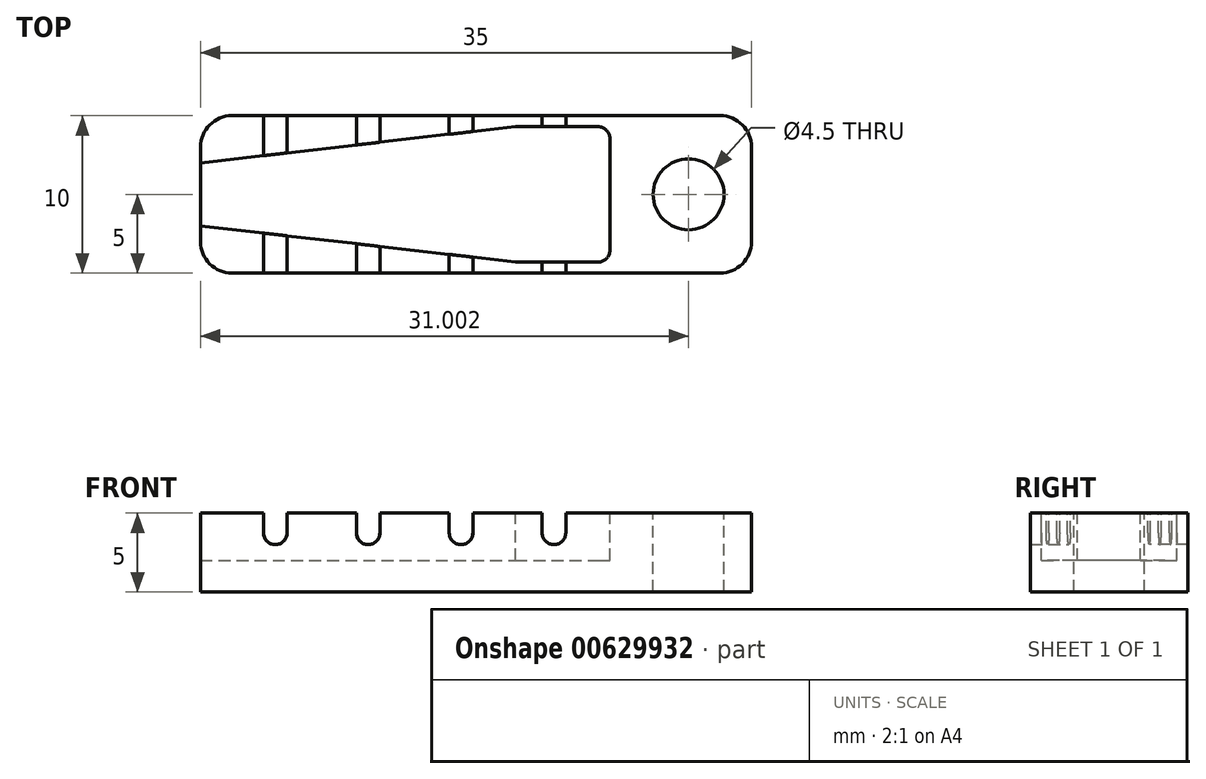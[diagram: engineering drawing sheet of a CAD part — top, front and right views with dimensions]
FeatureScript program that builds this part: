
annotation { "Feature Type Name" : "Feature", "Feature Type Description" : "" }
export const myFeature = defineFeature(function(context is Context, id is Id, definition is map)
    precondition{}
    {
        {
            var Q0;
            Q0=qCreatedBy(makeId("Top.planeOp"),FACE);
            var sketch = newSketch(context, id + "F0", { "sketchPlane" : qUnion([Q0])});
            skLineSegment(sketch, "E0.bottom", {"start": v(-22.89, 5) * mm, "end": v(12.11, 5) * mm});
            skLineSegment(sketch, "E0.top", {"start": v(-22.89, -5) * mm, "end": v(12.11, -5) * mm});
            skLineSegment(sketch, "E0.left", {"start": v(-22.89, 5) * mm, "end": v(-22.89, -5) * mm});
            skLineSegment(sketch, "E0.right", {"start": v(12.11, 5) * mm, "end": v(12.11, -5) * mm});
            skLineSegment(sketch, "E1", {"start": v(-22.89, 2) * mm, "end": v(-2.89, 4.3) * mm});
            skLineSegment(sketch, "E2.MirrorCS", {"start": v(-22.89, -2) * mm, "end": v(-2.89, -4.3) * mm});
            skLineSegment(sketch, "E3", {"start": v(-2.89, 4.3) * mm, "end": v(3.11, 4.3) * mm});
            skLineSegment(sketch, "E4.MirrorCS", {"start": v(-2.89, -4.3) * mm, "end": v(3.11, -4.3) * mm});
            skLineSegment(sketch, "E5", {"start": v(3.11, 4.3) * mm, "end": v(3.11, -4.3) * mm});
            skCircle(sketch, "E6", {"center": v(8.11, 0) * mm, "radius": 2.25 * mm});
            skLineSegment(sketch, "E7", {"start": v(-18.89, 5) * mm, "end": v(-18.89, -5) * mm});
            skLineSegment(sketch, "E8", {"start": v(-17.39, 5) * mm, "end": v(-17.39, -5) * mm});
            skLineSegment(sketch, "E9.1.0.0", {"start": v(-12.99, 5) * mm, "end": v(-12.99, -5) * mm});
            skLineSegment(sketch, "E9.1.0.1", {"start": v(-11.49, 5) * mm, "end": v(-11.49, -5) * mm});
            skLineSegment(sketch, "E9.2.0.0", {"start": v(-7.09, 5) * mm, "end": v(-7.09, -5) * mm});
            skLineSegment(sketch, "E9.2.0.1", {"start": v(-5.59, 5) * mm, "end": v(-5.59, -5) * mm});
            skLineSegment(sketch, "E9.3.0.0", {"start": v(-1.19, 5) * mm, "end": v(-1.19, -5) * mm});
            skLineSegment(sketch, "E9.3.0.1", {"start": v(0.31, 5) * mm, "end": v(0.31, -5) * mm});
            skLineSegment(sketch, "E9.direction1", {"start": v(-18.89, -5) * mm, "end": v(-12.99, -5) * mm, "construction": true});
            skSolve(sketch);
        }
        {
            var Q0;
            Q0 = qSketchRegion(id + "F0", true);
            var Q1;
            {var subQ0=sQuery(id+"F0.wireOp",EDGE,"E9.3.0.0");var subQ1=sQuery(id+"F0.wireOp",EDGE,"E3");var subQ2=makeQuery(id+"F0.imprint","INTERSECT",VERTEX,{"derivedFrom":[subQ1,subQ0]});Q1=makeQuery(id+"F0.imprint","IMPRINT",FACE,{"disambiguationData":[TD([[makeQuery(id+"F0.imprint","IMPRINT",EDGE,{"disambiguationData":[TD([[subQ2,-1.0]])],"derivedFrom":subQ1}),-1.0]])]});}
            var Q2;
            {var subQ0=sQuery(id+"F0.wireOp",EDGE,"E9.2.0.0");var subQ1=sQuery(id+"F0.wireOp",EDGE,"E1");var subQ2=makeQuery(id+"F0.imprint","INTERSECT",VERTEX,{"derivedFrom":[subQ1,subQ0]});Q2=makeQuery(id+"F0.imprint","IMPRINT",FACE,{"disambiguationData":[TD([[makeQuery(id+"F0.imprint","IMPRINT",EDGE,{"disambiguationData":[TD([[subQ2,-1.0]])],"derivedFrom":subQ1}),-1.0]])]});}
            var Q3;
            {var subQ0=sQuery(id+"F0.wireOp",EDGE,"E7");var subQ1=sQuery(id+"F0.wireOp",EDGE,"E1");var subQ2=makeQuery(id+"F0.imprint","INTERSECT",VERTEX,{"derivedFrom":[subQ1,subQ0]});Q3=makeQuery(id+"F0.imprint","IMPRINT",FACE,{"disambiguationData":[TD([[makeQuery(id+"F0.imprint","IMPRINT",EDGE,{"disambiguationData":[TD([[subQ2,-1.0]])],"derivedFrom":subQ1}),-1.0]])]});}
            var Q4;
            {var subQ0=sQuery(id+"F0.wireOp",EDGE,"E8");var subQ1=sQuery(id+"F0.wireOp",EDGE,"E1");var subQ2=makeQuery(id+"F0.imprint","INTERSECT",VERTEX,{"derivedFrom":[subQ1,subQ0]});Q4=makeQuery(id+"F0.imprint","IMPRINT",FACE,{"disambiguationData":[TD([[makeQuery(id+"F0.imprint","IMPRINT",EDGE,{"disambiguationData":[TD([[subQ2,-1.0]])],"derivedFrom":subQ1}),-1.0]])]});}
            var Q5;
            {var subQ0=sQuery(id+"F0.wireOp",EDGE,"E9.1.0.1");var subQ1=sQuery(id+"F0.wireOp",EDGE,"E1");var subQ2=makeQuery(id+"F0.imprint","INTERSECT",VERTEX,{"derivedFrom":[subQ1,subQ0]});Q5=makeQuery(id+"F0.imprint","IMPRINT",FACE,{"disambiguationData":[TD([[makeQuery(id+"F0.imprint","IMPRINT",EDGE,{"disambiguationData":[TD([[subQ2,-1.0]])],"derivedFrom":subQ1}),-1.0]])]});}
            var Q6;
            {var subQ0=sQuery(id+"F0.wireOp",EDGE,"E9.1.0.0");var subQ1=sQuery(id+"F0.wireOp",EDGE,"E1");var subQ2=makeQuery(id+"F0.imprint","INTERSECT",VERTEX,{"derivedFrom":[subQ1,subQ0]});Q6=makeQuery(id+"F0.imprint","IMPRINT",FACE,{"disambiguationData":[TD([[makeQuery(id+"F0.imprint","IMPRINT",EDGE,{"disambiguationData":[TD([[subQ2,-1.0]])],"derivedFrom":subQ1}),-1.0]])]});}
            var Q7;
            {var subQ5=sQuery(id+"F0.wireOp",EDGE,"E3");var subQ6=sQuery(id+"F0.wireOp",EDGE,"E1");var subQ7=makeQuery(id+"F0.imprint","INTERSECT",VERTEX,{"derivedFrom":[subQ6,subQ5]});Q7=makeQuery(id+"F0.imprint","IMPRINT",FACE,{"disambiguationData":[TD([[makeQuery(id+"F0.imprint","IMPRINT",EDGE,{"disambiguationData":[TD([[subQ7,1.0]])],"derivedFrom":subQ6}),-1.0]])]});}
            var Q8;
            {var subQ0=sQuery(id+"F0.wireOp",EDGE,"E5");Q8=makeQuery(id+"F0.imprint","IMPRINT",FACE,{"disambiguationData":[TD([[makeQuery(id+"F0.imprint","IMPRINT",EDGE,{"derivedFrom":subQ0}),-1.0]])]});}
            extrude(context, id + "F1", {"entities" : qUnion([Q0, Q1, Q2, Q3, Q4, Q5, Q6, Q7, Q8]), "depth" : -5 * mm, "offsetDistance" : 25 * mm});
        }
        {
            var Q0;
            {var subQ0=sQuery(id+"F0.wireOp",EDGE,"E1");var subQ1=sQuery(id+"F0.wireOp",EDGE,"E0.left");var subQ2=makeQuery(id+"F0.imprint","INTERSECT",VERTEX,{"derivedFrom":[subQ1,subQ0]});Q0=makeQuery(id+"F0.imprint","IMPRINT",FACE,{"disambiguationData":[TD([[makeQuery(id+"F0.imprint","IMPRINT",EDGE,{"disambiguationData":[TD([[subQ2,-1.0]])],"derivedFrom":subQ1}),1.0]])]});}
            var Q1;
            {var subQ0=sQuery(id+"F0.wireOp",EDGE,"E7");var subQ1=sQuery(id+"F0.wireOp",EDGE,"E1");var subQ2=makeQuery(id+"F0.imprint","INTERSECT",VERTEX,{"derivedFrom":[subQ1,subQ0]});Q1=makeQuery(id+"F0.imprint","IMPRINT",FACE,{"disambiguationData":[TD([[makeQuery(id+"F0.imprint","IMPRINT",EDGE,{"disambiguationData":[TD([[subQ2,-1.0]])],"derivedFrom":subQ1}),-1.0]])]});}
            var Q2;
            {var subQ0=sQuery(id+"F0.wireOp",EDGE,"E8");var subQ1=sQuery(id+"F0.wireOp",EDGE,"E1");var subQ2=makeQuery(id+"F0.imprint","INTERSECT",VERTEX,{"derivedFrom":[subQ1,subQ0]});Q2=makeQuery(id+"F0.imprint","IMPRINT",FACE,{"disambiguationData":[TD([[makeQuery(id+"F0.imprint","IMPRINT",EDGE,{"disambiguationData":[TD([[subQ2,-1.0]])],"derivedFrom":subQ1}),-1.0]])]});}
            var Q3;
            {var subQ0=sQuery(id+"F0.wireOp",EDGE,"E9.1.0.0");var subQ1=sQuery(id+"F0.wireOp",EDGE,"E1");var subQ2=makeQuery(id+"F0.imprint","INTERSECT",VERTEX,{"derivedFrom":[subQ1,subQ0]});Q3=makeQuery(id+"F0.imprint","IMPRINT",FACE,{"disambiguationData":[TD([[makeQuery(id+"F0.imprint","IMPRINT",EDGE,{"disambiguationData":[TD([[subQ2,-1.0]])],"derivedFrom":subQ1}),-1.0]])]});}
            var Q4;
            {var subQ0=sQuery(id+"F0.wireOp",EDGE,"E9.1.0.1");var subQ1=sQuery(id+"F0.wireOp",EDGE,"E1");var subQ2=makeQuery(id+"F0.imprint","INTERSECT",VERTEX,{"derivedFrom":[subQ1,subQ0]});Q4=makeQuery(id+"F0.imprint","IMPRINT",FACE,{"disambiguationData":[TD([[makeQuery(id+"F0.imprint","IMPRINT",EDGE,{"disambiguationData":[TD([[subQ2,-1.0]])],"derivedFrom":subQ1}),-1.0]])]});}
            var Q5;
            {var subQ0=sQuery(id+"F0.wireOp",EDGE,"E9.2.0.0");var subQ1=sQuery(id+"F0.wireOp",EDGE,"E1");var subQ2=makeQuery(id+"F0.imprint","INTERSECT",VERTEX,{"derivedFrom":[subQ1,subQ0]});Q5=makeQuery(id+"F0.imprint","IMPRINT",FACE,{"disambiguationData":[TD([[makeQuery(id+"F0.imprint","IMPRINT",EDGE,{"disambiguationData":[TD([[subQ2,-1.0]])],"derivedFrom":subQ1}),-1.0]])]});}
            var Q6;
            {var subQ5=sQuery(id+"F0.wireOp",EDGE,"E3");var subQ6=sQuery(id+"F0.wireOp",EDGE,"E1");var subQ7=makeQuery(id+"F0.imprint","INTERSECT",VERTEX,{"derivedFrom":[subQ6,subQ5]});Q6=makeQuery(id+"F0.imprint","IMPRINT",FACE,{"disambiguationData":[TD([[makeQuery(id+"F0.imprint","IMPRINT",EDGE,{"disambiguationData":[TD([[subQ7,1.0]])],"derivedFrom":subQ6}),-1.0]])]});}
            var Q7;
            {var subQ0=sQuery(id+"F0.wireOp",EDGE,"E9.3.0.0");var subQ1=sQuery(id+"F0.wireOp",EDGE,"E3");var subQ2=makeQuery(id+"F0.imprint","INTERSECT",VERTEX,{"derivedFrom":[subQ1,subQ0]});Q7=makeQuery(id+"F0.imprint","IMPRINT",FACE,{"disambiguationData":[TD([[makeQuery(id+"F0.imprint","IMPRINT",EDGE,{"disambiguationData":[TD([[subQ2,-1.0]])],"derivedFrom":subQ1}),-1.0]])]});}
            var Q8;
            {var subQ0=sQuery(id+"F0.wireOp",EDGE,"E5");Q8=makeQuery(id+"F0.imprint","IMPRINT",FACE,{"disambiguationData":[TD([[makeQuery(id+"F0.imprint","IMPRINT",EDGE,{"derivedFrom":subQ0}),-1.0]])]});}
            extrude(context, id + "F2", {"entities" : qUnion([Q0, Q1, Q2, Q3, Q4, Q5, Q6, Q7, Q8]), "operationType" : NewBodyOperationType.REMOVE, "depth" : -3 * mm, "offsetDistance" : 25 * mm});
        }
        {
            var Q0;
            {var subQ0=sQuery(id+"F0.wireOp",EDGE,"E7");var subQ1=sQuery(id+"F0.wireOp",EDGE,"E0.bottom");var subQ2=makeQuery(id+"F0.imprint","INTERSECT",VERTEX,{"derivedFrom":[subQ1,subQ0]});Q0=makeQuery(id+"F0.imprint","IMPRINT",FACE,{"disambiguationData":[TD([[makeQuery(id+"F0.imprint","IMPRINT",EDGE,{"disambiguationData":[TD([[subQ2,-1.0]])],"derivedFrom":subQ1}),-1.0]])]});}
            var Q1;
            {var subQ0=sQuery(id+"F0.wireOp",EDGE,"E9.1.0.0");var subQ1=sQuery(id+"F0.wireOp",EDGE,"E0.bottom");var subQ2=makeQuery(id+"F0.imprint","INTERSECT",VERTEX,{"derivedFrom":[subQ1,subQ0]});Q1=makeQuery(id+"F0.imprint","IMPRINT",FACE,{"disambiguationData":[TD([[makeQuery(id+"F0.imprint","IMPRINT",EDGE,{"disambiguationData":[TD([[subQ2,-1.0]])],"derivedFrom":subQ1}),-1.0]])]});}
            var Q2;
            {var subQ0=sQuery(id+"F0.wireOp",EDGE,"E9.2.0.0");var subQ1=sQuery(id+"F0.wireOp",EDGE,"E0.bottom");var subQ2=makeQuery(id+"F0.imprint","INTERSECT",VERTEX,{"derivedFrom":[subQ1,subQ0]});Q2=makeQuery(id+"F0.imprint","IMPRINT",FACE,{"disambiguationData":[TD([[makeQuery(id+"F0.imprint","IMPRINT",EDGE,{"disambiguationData":[TD([[subQ2,-1.0]])],"derivedFrom":subQ1}),-1.0]])]});}
            var Q3;
            {var subQ0=sQuery(id+"F0.wireOp",EDGE,"E9.3.0.0");var subQ1=sQuery(id+"F0.wireOp",EDGE,"E0.top");var subQ2=makeQuery(id+"F0.imprint","INTERSECT",VERTEX,{"derivedFrom":[subQ1,subQ0]});Q3=makeQuery(id+"F0.imprint","IMPRINT",FACE,{"disambiguationData":[TD([[makeQuery(id+"F0.imprint","IMPRINT",EDGE,{"disambiguationData":[TD([[subQ2,-1.0]])],"derivedFrom":subQ1}),1.0]])]});}
            var Q4;
            {var subQ0=sQuery(id+"F0.wireOp",EDGE,"E7");var subQ1=sQuery(id+"F0.wireOp",EDGE,"E0.top");var subQ2=makeQuery(id+"F0.imprint","INTERSECT",VERTEX,{"derivedFrom":[subQ1,subQ0]});Q4=makeQuery(id+"F0.imprint","IMPRINT",FACE,{"disambiguationData":[TD([[makeQuery(id+"F0.imprint","IMPRINT",EDGE,{"disambiguationData":[TD([[subQ2,-1.0]])],"derivedFrom":subQ1}),1.0]])]});}
            var Q5;
            {var subQ0=sQuery(id+"F0.wireOp",EDGE,"E9.1.0.0");var subQ1=sQuery(id+"F0.wireOp",EDGE,"E0.top");var subQ2=makeQuery(id+"F0.imprint","INTERSECT",VERTEX,{"derivedFrom":[subQ1,subQ0]});Q5=makeQuery(id+"F0.imprint","IMPRINT",FACE,{"disambiguationData":[TD([[makeQuery(id+"F0.imprint","IMPRINT",EDGE,{"disambiguationData":[TD([[subQ2,-1.0]])],"derivedFrom":subQ1}),1.0]])]});}
            var Q6;
            {var subQ0=sQuery(id+"F0.wireOp",EDGE,"E9.2.0.0");var subQ1=sQuery(id+"F0.wireOp",EDGE,"E0.top");var subQ2=makeQuery(id+"F0.imprint","INTERSECT",VERTEX,{"derivedFrom":[subQ1,subQ0]});Q6=makeQuery(id+"F0.imprint","IMPRINT",FACE,{"disambiguationData":[TD([[makeQuery(id+"F0.imprint","IMPRINT",EDGE,{"disambiguationData":[TD([[subQ2,-1.0]])],"derivedFrom":subQ1}),1.0]])]});}
            var Q7;
            {var subQ0=sQuery(id+"F0.wireOp",EDGE,"E9.3.0.0");var subQ1=sQuery(id+"F0.wireOp",EDGE,"E0.bottom");var subQ2=makeQuery(id+"F0.imprint","INTERSECT",VERTEX,{"derivedFrom":[subQ1,subQ0]});Q7=makeQuery(id+"F0.imprint","IMPRINT",FACE,{"disambiguationData":[TD([[makeQuery(id+"F0.imprint","IMPRINT",EDGE,{"disambiguationData":[TD([[subQ2,-1.0]])],"derivedFrom":subQ1}),-1.0]])]});}
            extrude(context, id + "F3", {"entities" : qUnion([Q0, Q1, Q2, Q3, Q4, Q5, Q6, Q7]), "operationType" : NewBodyOperationType.REMOVE, "oppositeDirection" : true, "depth" : 2 * mm, "offsetDistance" : 25 * mm});
        }
        {
            var Q0;
            {var subQ0=sQuery(id+"F0.wireOp",EDGE,"E8");Q0=makeQuery(id+"F3.boolean.opBoolean","COPY",EDGE,{"derivedFrom":makeQuery(id+"F3.opExtrude","CAP_EDGE",EDGE,{"disambiguationData":[OSD([subQ0]),TDD([makeQuery(id+"F0.imprint","IMPRINT",EDGE,{"disambiguationData":[TD([[makeQuery(id+"F0.imprint","INTERSECT",VERTEX,{"derivedFrom":[sQuery(id+"F0.wireOp",EDGE,"E0.top"),subQ0]}),1.0]])],"derivedFrom":subQ0})])],"isStart":false})});}
            var Q1;
            {var subQ0=sQuery(id+"F0.wireOp",EDGE,"E9.1.0.1");Q1=makeQuery(id+"F3.boolean.opBoolean","COPY",EDGE,{"derivedFrom":makeQuery(id+"F3.opExtrude","CAP_EDGE",EDGE,{"disambiguationData":[OSD([subQ0]),TDD([makeQuery(id+"F0.imprint","IMPRINT",EDGE,{"disambiguationData":[TD([[makeQuery(id+"F0.imprint","INTERSECT",VERTEX,{"derivedFrom":[sQuery(id+"F0.wireOp",EDGE,"E0.top"),subQ0]}),1.0]])],"derivedFrom":subQ0})])],"isStart":false})});}
            var Q2;
            {var subQ0=sQuery(id+"F0.wireOp",EDGE,"E9.2.0.1");Q2=makeQuery(id+"F3.boolean.opBoolean","COPY",EDGE,{"derivedFrom":makeQuery(id+"F3.opExtrude","CAP_EDGE",EDGE,{"disambiguationData":[OSD([subQ0]),TDD([makeQuery(id+"F0.imprint","IMPRINT",EDGE,{"disambiguationData":[TD([[makeQuery(id+"F0.imprint","INTERSECT",VERTEX,{"derivedFrom":[sQuery(id+"F0.wireOp",EDGE,"E0.top"),subQ0]}),1.0]])],"derivedFrom":subQ0})])],"isStart":false})});}
            var Q3;
            {var subQ0=sQuery(id+"F0.wireOp",EDGE,"E9.3.0.1");Q3=makeQuery(id+"F3.boolean.opBoolean","COPY",EDGE,{"derivedFrom":makeQuery(id+"F3.opExtrude","CAP_EDGE",EDGE,{"disambiguationData":[OSD([subQ0]),TDD([makeQuery(id+"F0.imprint","IMPRINT",EDGE,{"disambiguationData":[TD([[makeQuery(id+"F0.imprint","INTERSECT",VERTEX,{"derivedFrom":[sQuery(id+"F0.wireOp",EDGE,"E0.top"),subQ0]}),1.0]])],"derivedFrom":subQ0})])],"isStart":false})});}
            var Q4;
            {var subQ0=sQuery(id+"F0.wireOp",EDGE,"E7");Q4=makeQuery(id+"F3.boolean.opBoolean","COPY",EDGE,{"derivedFrom":makeQuery(id+"F3.opExtrude","CAP_EDGE",EDGE,{"disambiguationData":[OSD([subQ0]),TDD([makeQuery(id+"F0.imprint","IMPRINT",EDGE,{"disambiguationData":[TD([[makeQuery(id+"F0.imprint","INTERSECT",VERTEX,{"derivedFrom":[sQuery(id+"F0.wireOp",EDGE,"E0.top"),subQ0]}),1.0]])],"derivedFrom":subQ0})])],"isStart":false})});}
            var Q5;
            {var subQ0=sQuery(id+"F0.wireOp",EDGE,"E9.1.0.0");Q5=makeQuery(id+"F3.boolean.opBoolean","COPY",EDGE,{"derivedFrom":makeQuery(id+"F3.opExtrude","CAP_EDGE",EDGE,{"disambiguationData":[OSD([subQ0]),TDD([makeQuery(id+"F0.imprint","IMPRINT",EDGE,{"disambiguationData":[TD([[makeQuery(id+"F0.imprint","INTERSECT",VERTEX,{"derivedFrom":[sQuery(id+"F0.wireOp",EDGE,"E0.top"),subQ0]}),1.0]])],"derivedFrom":subQ0})])],"isStart":false})});}
            var Q6;
            {var subQ0=sQuery(id+"F0.wireOp",EDGE,"E9.2.0.0");Q6=makeQuery(id+"F3.boolean.opBoolean","COPY",EDGE,{"derivedFrom":makeQuery(id+"F3.opExtrude","CAP_EDGE",EDGE,{"disambiguationData":[OSD([subQ0]),TDD([makeQuery(id+"F0.imprint","IMPRINT",EDGE,{"disambiguationData":[TD([[makeQuery(id+"F0.imprint","INTERSECT",VERTEX,{"derivedFrom":[sQuery(id+"F0.wireOp",EDGE,"E0.top"),subQ0]}),1.0]])],"derivedFrom":subQ0})])],"isStart":false})});}
            var Q7;
            {var subQ0=sQuery(id+"F0.wireOp",EDGE,"E9.3.0.0");Q7=makeQuery(id+"F3.boolean.opBoolean","COPY",EDGE,{"derivedFrom":makeQuery(id+"F3.opExtrude","CAP_EDGE",EDGE,{"disambiguationData":[OSD([subQ0]),TDD([makeQuery(id+"F0.imprint","IMPRINT",EDGE,{"disambiguationData":[TD([[makeQuery(id+"F0.imprint","INTERSECT",VERTEX,{"derivedFrom":[sQuery(id+"F0.wireOp",EDGE,"E0.top"),subQ0]}),1.0]])],"derivedFrom":subQ0})])],"isStart":false})});}
            var Q8;
            {var subQ0=sQuery(id+"F0.wireOp",EDGE,"E7");Q8=makeQuery(id+"F3.boolean.opBoolean","COPY",EDGE,{"derivedFrom":makeQuery(id+"F3.opExtrude","CAP_EDGE",EDGE,{"disambiguationData":[OSD([subQ0]),TDD([makeQuery(id+"F0.imprint","IMPRINT",EDGE,{"disambiguationData":[TD([[makeQuery(id+"F0.imprint","INTERSECT",VERTEX,{"derivedFrom":[sQuery(id+"F0.wireOp",EDGE,"E0.bottom"),subQ0]}),-1.0]])],"derivedFrom":subQ0})])],"isStart":false})});}
            var Q9;
            {var subQ0=sQuery(id+"F0.wireOp",EDGE,"E9.1.0.0");Q9=makeQuery(id+"F3.boolean.opBoolean","COPY",EDGE,{"derivedFrom":makeQuery(id+"F3.opExtrude","CAP_EDGE",EDGE,{"disambiguationData":[OSD([subQ0]),TDD([makeQuery(id+"F0.imprint","IMPRINT",EDGE,{"disambiguationData":[TD([[makeQuery(id+"F0.imprint","INTERSECT",VERTEX,{"derivedFrom":[sQuery(id+"F0.wireOp",EDGE,"E0.bottom"),subQ0]}),-1.0]])],"derivedFrom":subQ0})])],"isStart":false})});}
            var Q10;
            {var subQ0=sQuery(id+"F0.wireOp",EDGE,"E9.2.0.0");Q10=makeQuery(id+"F3.boolean.opBoolean","COPY",EDGE,{"derivedFrom":makeQuery(id+"F3.opExtrude","CAP_EDGE",EDGE,{"disambiguationData":[OSD([subQ0]),TDD([makeQuery(id+"F0.imprint","IMPRINT",EDGE,{"disambiguationData":[TD([[makeQuery(id+"F0.imprint","INTERSECT",VERTEX,{"derivedFrom":[sQuery(id+"F0.wireOp",EDGE,"E0.bottom"),subQ0]}),-1.0]])],"derivedFrom":subQ0})])],"isStart":false})});}
            var Q11;
            {var subQ0=sQuery(id+"F0.wireOp",EDGE,"E9.3.0.0");Q11=makeQuery(id+"F3.boolean.opBoolean","COPY",EDGE,{"derivedFrom":makeQuery(id+"F3.opExtrude","CAP_EDGE",EDGE,{"disambiguationData":[OSD([subQ0]),TDD([makeQuery(id+"F0.imprint","IMPRINT",EDGE,{"disambiguationData":[TD([[makeQuery(id+"F0.imprint","INTERSECT",VERTEX,{"derivedFrom":[sQuery(id+"F0.wireOp",EDGE,"E0.bottom"),subQ0]}),-1.0]])],"derivedFrom":subQ0})])],"isStart":false})});}
            var Q12;
            {var subQ0=sQuery(id+"F0.wireOp",EDGE,"E8");Q12=makeQuery(id+"F3.boolean.opBoolean","COPY",EDGE,{"derivedFrom":makeQuery(id+"F3.opExtrude","CAP_EDGE",EDGE,{"disambiguationData":[OSD([subQ0]),TDD([makeQuery(id+"F0.imprint","IMPRINT",EDGE,{"disambiguationData":[TD([[makeQuery(id+"F0.imprint","INTERSECT",VERTEX,{"derivedFrom":[sQuery(id+"F0.wireOp",EDGE,"E0.bottom"),subQ0]}),-1.0]])],"derivedFrom":subQ0})])],"isStart":false})});}
            var Q13;
            {var subQ0=sQuery(id+"F0.wireOp",EDGE,"E9.1.0.1");Q13=makeQuery(id+"F3.boolean.opBoolean","COPY",EDGE,{"derivedFrom":makeQuery(id+"F3.opExtrude","CAP_EDGE",EDGE,{"disambiguationData":[OSD([subQ0]),TDD([makeQuery(id+"F0.imprint","IMPRINT",EDGE,{"disambiguationData":[TD([[makeQuery(id+"F0.imprint","INTERSECT",VERTEX,{"derivedFrom":[sQuery(id+"F0.wireOp",EDGE,"E0.bottom"),subQ0]}),-1.0]])],"derivedFrom":subQ0})])],"isStart":false})});}
            var Q14;
            {var subQ0=sQuery(id+"F0.wireOp",EDGE,"E9.2.0.1");Q14=makeQuery(id+"F3.boolean.opBoolean","COPY",EDGE,{"derivedFrom":makeQuery(id+"F3.opExtrude","CAP_EDGE",EDGE,{"disambiguationData":[OSD([subQ0]),TDD([makeQuery(id+"F0.imprint","IMPRINT",EDGE,{"disambiguationData":[TD([[makeQuery(id+"F0.imprint","INTERSECT",VERTEX,{"derivedFrom":[sQuery(id+"F0.wireOp",EDGE,"E0.bottom"),subQ0]}),-1.0]])],"derivedFrom":subQ0})])],"isStart":false})});}
            var Q15;
            {var subQ0=sQuery(id+"F0.wireOp",EDGE,"E9.3.0.1");Q15=makeQuery(id+"F3.boolean.opBoolean","COPY",EDGE,{"derivedFrom":makeQuery(id+"F3.opExtrude","CAP_EDGE",EDGE,{"disambiguationData":[OSD([subQ0]),TDD([makeQuery(id+"F0.imprint","IMPRINT",EDGE,{"disambiguationData":[TD([[makeQuery(id+"F0.imprint","INTERSECT",VERTEX,{"derivedFrom":[sQuery(id+"F0.wireOp",EDGE,"E0.bottom"),subQ0]}),-1.0]])],"derivedFrom":subQ0})])],"isStart":false})});}
            var Q16;
            Q16=makeQuery(id+"F2.boolean.opBoolean","COPY",EDGE,{"derivedFrom":makeQuery(id+"F2.opExtrude","SWEPT_EDGE",EDGE,{"disambiguationData":[OSD([sQuery(id+"F0.wireOp",EDGE,"E3"),sQuery(id+"F0.wireOp",EDGE,"E5")])]})});
            var Q17;
            Q17=makeQuery(id+"F2.boolean.opBoolean","COPY",EDGE,{"derivedFrom":makeQuery(id+"F2.opExtrude","SWEPT_EDGE",EDGE,{"disambiguationData":[OSD([sQuery(id+"F0.wireOp",EDGE,"E4.MirrorCS"),sQuery(id+"F0.wireOp",EDGE,"E5")])]})});
            fillet(context, id + "F4", {"entities" : qUnion([Q0, Q1, Q2, Q3, Q4, Q5, Q6, Q7, Q8, Q9, Q10, Q11, Q12, Q13, Q14, Q15, Q16, Q17]), "radius" : .75 * mm, "tangentPropagation" : true, "allowEdgeOverflow" : false});
        }
        {
            var Q0;
            Q0=makeQuery(id+"F1.opExtrude","SWEPT_EDGE",EDGE,{"disambiguationData":[OSD([sQuery(id+"F0.wireOp",EDGE,"E0.top"),sQuery(id+"F0.wireOp",EDGE,"E0.left")])]});
            var Q1;
            Q1=makeQuery(id+"F1.opExtrude","SWEPT_EDGE",EDGE,{"disambiguationData":[OSD([sQuery(id+"F0.wireOp",EDGE,"E0.bottom"),sQuery(id+"F0.wireOp",EDGE,"E0.left")])]});
            var Q2;
            Q2=makeQuery(id+"F1.opExtrude","SWEPT_EDGE",EDGE,{"disambiguationData":[OSD([sQuery(id+"F0.wireOp",EDGE,"E0.top"),sQuery(id+"F0.wireOp",EDGE,"E0.right")])]});
            var Q3;
            Q3=makeQuery(id+"F1.opExtrude","SWEPT_EDGE",EDGE,{"disambiguationData":[OSD([sQuery(id+"F0.wireOp",EDGE,"E0.bottom"),sQuery(id+"F0.wireOp",EDGE,"E0.right")])]});
            fillet(context, id + "F5", {"entities" : qUnion([Q0, Q1, Q2, Q3]), "radius" : 2 * mm, "tangentPropagation" : true, "allowEdgeOverflow" : false});
        }
    });
